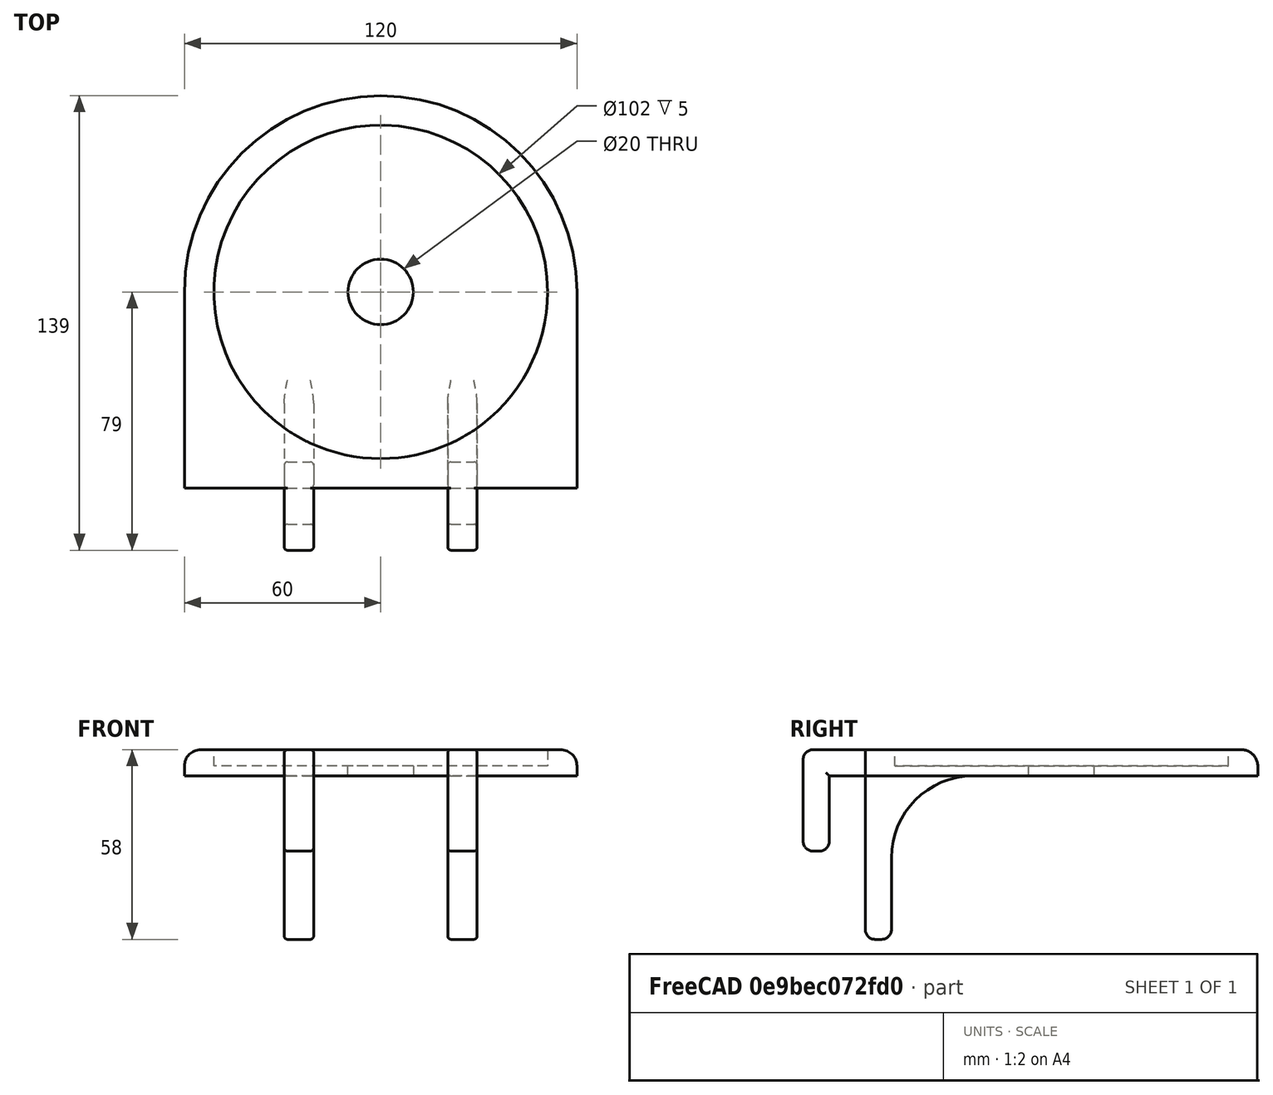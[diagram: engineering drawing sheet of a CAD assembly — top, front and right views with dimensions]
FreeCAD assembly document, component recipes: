
FREECAD ASSEMBLY — COMPONENT RECIPES ("DollStand")

This assembly document has 2 components, labeled P0..P1 below (a component is one placed body or linked part). 2 of them carry a construction recipe — the FreeCAD feature program that regenerates the part from scratch, quoted from this document or its linked companion documents; the rest are supplied as boundary geometry only. No exploded tour is included for this assembly.
COMPONENT P0 — recipe-attached ("PlateauBody", modeled in this document).
Construction recipe (the document's own serialized feature program — sketch geometry with constraints, then the solid features built on it; lengths are millimeters unless a unit is written):

FEATURE [Sketcher::SketchObject] Sketch001  label="PlateauBodySketch"
  FullyConstrained = true
  MapMode = 5
  Support = -> [XY_Plane002]
  sketch-geometry (4):
    g0: ArcOfCircle CenterX=0 CenterY=79 CenterZ=0 NormalX=0 NormalY=0 NormalZ=1 AngleXU=0 Radius=60 StartAngle=0 EndAngle=3.14159
    g1: LineSegment StartX=-60 StartY=79 StartZ=0 EndX=-60 EndY=19 EndZ=0
    g2: LineSegment StartX=-60 StartY=19 StartZ=0 EndX=60 EndY=19 EndZ=0
    g3: LineSegment StartX=60 StartY=19 StartZ=0 EndX=60 EndY=79 EndZ=0
  constraints (12):
    c: PointOnObject(g0,g-2)
    c: Horizontal(g0,g0)
    c: Horizontal(g0,g0)
    c: Tangent(g0,g1) = -1.5708
    c: Coincident(g1,g2)
    c: Horizontal(g2)
    c: Coincident(g2,g3)
    c: Coincident(g3,g0)
    c: Vertical(g3)
    c: Diameter(g0) = 120
    c: DistanceY(g-1,g1) = 19
    c: DistanceY(g1,g1) = 60
FEATURE [PartDesign::Pad] Pad001  label="PlateauPad"
  Direction = (0,0,1)
  Length = 8
  Length2 = 10
  Profile = -> Sketch001
  ReferenceAxis = -> Sketch001 [N_Axis]
  Reversed = true
  Type = 0
FEATURE [PartDesign::Body] Body001  label="PlateauBody"
  Group = -> [Sketch001,Pad001]
  Origin = -> Origin002
  Tip = -> Pad001
COMPONENT P1 — recipe-attached ("HookBody001", modeled in this document).
Construction recipe (the document's own serialized feature program — sketch geometry with constraints, then the solid features built on it; lengths are millimeters unless a unit is written):

FEATURE [Sketcher::SketchObject] Sketch  label="HookSketch"
  FullyConstrained = true
  MapMode = 5
  Placement = pos=(0,0,0) rot=(0.57735,0.57735,0.57735;2.0944rad)
  Support = -> [YZ_Plane001]
  sketch-geometry (28):
    g0: LineSegment StartX=3 StartY=0 StartZ=0 EndX=66 EndY=0 EndZ=0
    g1: LineSegment StartX=69 StartY=-3 StartZ=0 EndX=69 EndY=-5 EndZ=0
    g2: LineSegment StartX=66 StartY=-8 StartZ=0 EndX=52 EndY=-8 EndZ=0
    g3: LineSegment StartX=27 StartY=-33 StartZ=0 EndX=27 EndY=-55 EndZ=0
    g4: LineSegment StartX=24 StartY=-58 StartZ=0 EndX=22 EndY=-58 EndZ=0
    g5: LineSegment StartX=19 StartY=-55 StartZ=0 EndX=19 EndY=-8 EndZ=0
    g6: LineSegment StartX=19 StartY=-8 StartZ=0 EndX=8 EndY=-8 EndZ=0
    g7: LineSegment StartX=8 StartY=-8 StartZ=0 EndX=8 EndY=-28 EndZ=0
    g8: LineSegment StartX=5 StartY=-31 StartZ=0 EndX=3 EndY=-31 EndZ=0
    g9: LineSegment StartX=0 StartY=-28 StartZ=0 EndX=0 EndY=-3 EndZ=0
    g10: ArcOfCircle CenterX=3 CenterY=-3 CenterZ=0 NormalX=0 NormalY=0 NormalZ=1 AngleXU=0 Radius=3 StartAngle=1.5708 EndAngle=3.14159
    g11: GeomPoint X=0 Y=0 Z=0
    g12: ArcOfCircle CenterX=66 CenterY=-3 CenterZ=0 NormalX=0 NormalY=0 NormalZ=1 AngleXU=0 Radius=3 StartAngle=0 EndAngle=1.5708
    g13: GeomPoint X=69 Y=0 Z=0
    g14: ArcOfCircle CenterX=66 CenterY=-5 CenterZ=0 NormalX=0 NormalY=0 NormalZ=1 AngleXU=0 Radius=3 StartAngle=4.71239 EndAngle=6.28319
    g15: GeomPoint X=69 Y=-8 Z=0
    g16: ArcOfCircle CenterX=52 CenterY=-33 CenterZ=0 NormalX=0 NormalY=0 NormalZ=1 AngleXU=0 Radius=25 StartAngle=1.5708 EndAngle=3.14159
    g17: GeomPoint X=27 Y=-8 Z=0
    g18: ArcOfCircle CenterX=24 CenterY=-55 CenterZ=0 NormalX=0 NormalY=0 NormalZ=1 AngleXU=0 Radius=3 StartAngle=4.71239 EndAngle=6.28319
    g19: GeomPoint X=27 Y=-58 Z=0
    g20: ArcOfCircle CenterX=22 CenterY=-55 CenterZ=0 NormalX=0 NormalY=0 NormalZ=1 AngleXU=0 Radius=3 StartAngle=3.14159 EndAngle=4.71239
    g21: GeomPoint X=19 Y=-58 Z=0
    g22: GeomPoint X=19 Y=-8 Z=0
    g23: GeomPoint X=8 Y=-8 Z=0
    g24: ArcOfCircle CenterX=5 CenterY=-28 CenterZ=0 NormalX=0 NormalY=0 NormalZ=1 AngleXU=0 Radius=3 StartAngle=4.71239 EndAngle=6.28319
    g25: GeomPoint X=8 Y=-31 Z=0
    g26: ArcOfCircle CenterX=3 CenterY=-28 CenterZ=0 NormalX=0 NormalY=0 NormalZ=1 AngleXU=0 Radius=3 StartAngle=3.14159 EndAngle=4.71239
    g27: GeomPoint X=0 Y=-31 Z=0
  constraints (64):
    c: Coincident(g-1,g11)
    c: PointOnObject(g13,g-1)
    c: Vertical(g1)
    c: Horizontal(g2)
    c: Vertical(g3)
    c: Horizontal(g4)
    c: Vertical(g5)
    c: Horizontal(g6)
    c: Vertical(g7)
    c: PointOnObject(g27,g-2)
    c: Horizontal(g8)
    c: DistanceX(g21,g19) = 8
    c: DistanceX(g27,g25) = 8
    c: DistanceY(g19,g17) = 50
    c: DistanceY(g25,g23) = 23
    c: DistanceY(g15,g13) = 8
    c: DistanceY(g27,g11) = 31
    c: PointOnObject(g11,g9)
    c: PointOnObject(g11,g0)
    c: Tangent(g9,g10) = 1.5708
    c: Tangent(g0,g10) = 1.5708
    c: PointOnObject(g13,g0)
    c: PointOnObject(g13,g1)
    c: Tangent(g0,g12) = 1.5708
    c: Tangent(g1,g12) = 1.5708
    c: PointOnObject(g15,g1)
    c: PointOnObject(g15,g2)
    c: Tangent(g1,g14) = 1.5708
    c: Tangent(g2,g14) = 1.5708
    c: PointOnObject(g17,g2)
    c: PointOnObject(g17,g3)
    c: Tangent(g2,g16) = -1.5708
    c: Tangent(g3,g16) = -1.5708
    c: PointOnObject(g19,g3)
    c: PointOnObject(g19,g4)
    c: Tangent(g3,g18) = 1.5708
    c: Tangent(g4,g18) = 1.5708
    c: PointOnObject(g21,g4)
    c: PointOnObject(g21,g5)
    c: Tangent(g4,g20) = 1.5708
    c: Tangent(g5,g20) = 1.5708
    c: PointOnObject(g22,g5)
    c: PointOnObject(g22,g6)
    c: PointOnObject(g25,g7)
    c: PointOnObject(g25,g8)
    c: Tangent(g7,g24) = 1.5708
    c: Tangent(g8,g24) = 1.5708
    c: PointOnObject(g27,g8)
    c: PointOnObject(g27,g9)
    c: Tangent(g8,g26) = 1.5708
    c: Tangent(g9,g26) = 1.5708
    c: Equal(g10,g12)
    c: Equal(g10,g14)
    c: Equal(g10,g18)
    c: Equal(g10,g20)
    c: Equal(g10,g24)
    c: Equal(g10,g26)
    c: Radius(g10) = 3
    c: Radius(g16) = 25
    c: DistanceX(g6,g6) = 11
    c: Coincident(g7,g23)
    c: Coincident(g5,g6)
    c: Coincident(g7,g6)
    c: DistanceX(g5,g1) = 50
FEATURE [PartDesign::Pad] Pad  label="HookPad"
  Direction = (1,-2e-16,3e-16)
  Length = 9
  Length2 = 10
  Midplane = true
  Placement = pos=(0,0,0) rot=(0.57735,0.57735,0.57735;2.0944rad)
  Profile = -> Sketch
  ReferenceAxis = -> Sketch [N_Axis]
  Type = 0
FEATURE [PartDesign::Fillet] Fillet  label="HookBodyFillet"
  Base = -> Pad [Face20,Face19]
  BaseFeature = -> Pad
  Placement = pos=(0,0,0) rot=(0.57735,0.57735,0.57735;2.0944rad)
  Radius = 1
  SupportTransform = false
  UseAllEdges = false
FEATURE [PartDesign::Body] Body  label="HookBody"
  Group = -> [Sketch,Pad,Fillet]
  Origin = -> Origin001
  Placement = pos=(-25,0,0) rot=(0,0,1;0rad)
  Tip = -> Fillet
PROVENANCE & LICENSES
A FreeCAD (.FCStd) document from a public repository crawl; recipes are the document's own serialized feature recipes (and, for linked parts, companion documents' recipes).
License: other.
